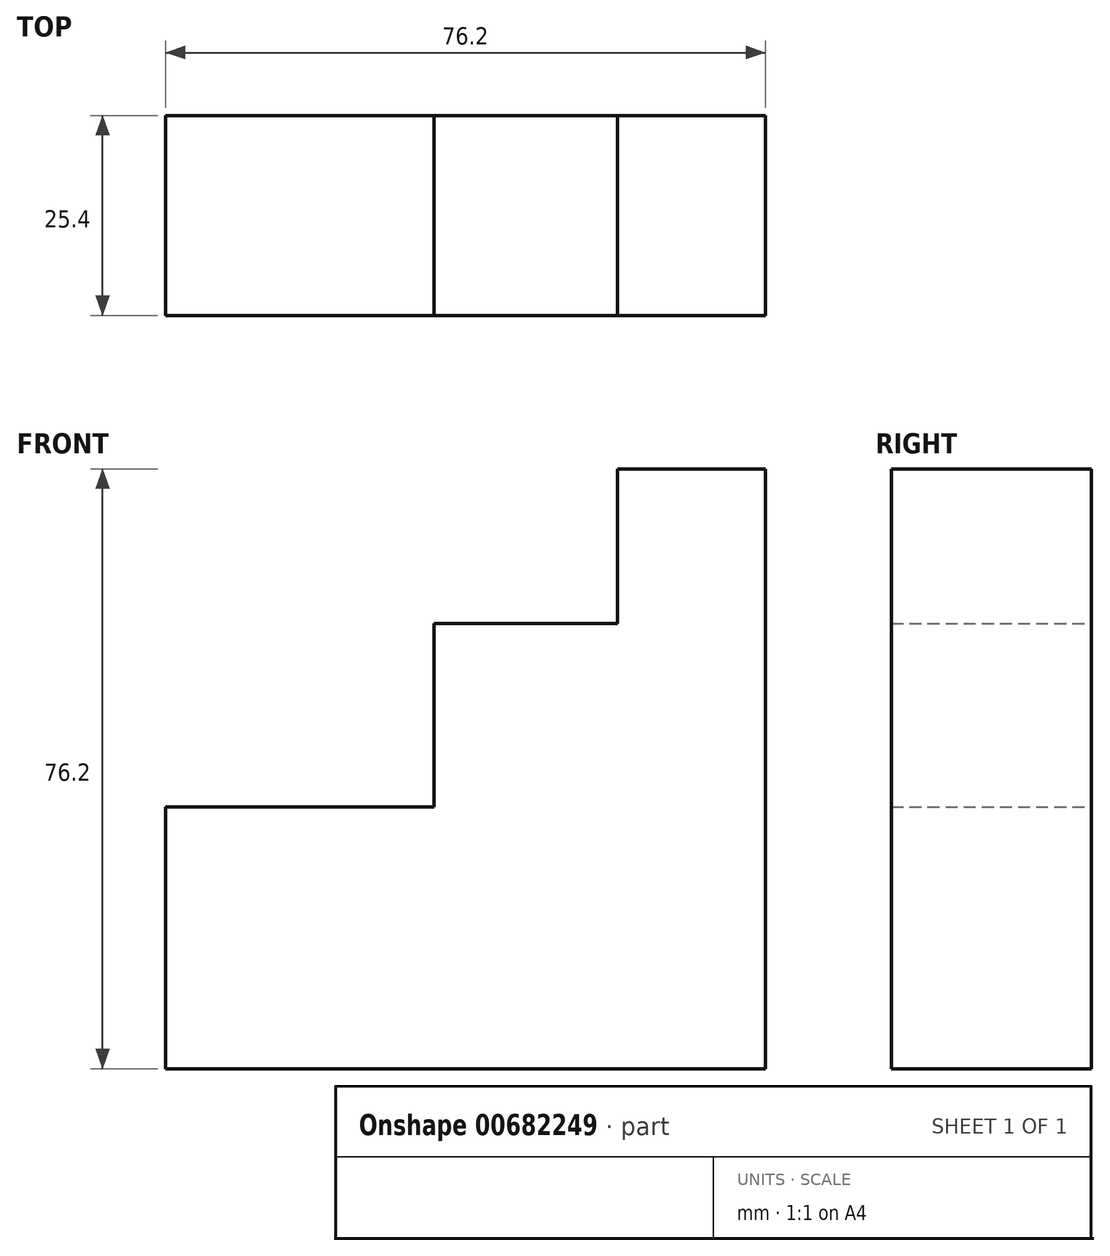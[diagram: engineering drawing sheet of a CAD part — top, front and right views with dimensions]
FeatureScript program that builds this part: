
annotation { "Feature Type Name" : "Feature", "Feature Type Description" : "" }
export const myFeature = defineFeature(function(context is Context, id is Id, definition is map)
    precondition{}
    {
        {
            var Q0;
            Q0=qCreatedBy(makeId("Front.planeOp"),FACE);
            var sketch = newSketch(context, id + "F0", { "sketchPlane" : qUnion([Q0])});
            skLineSegment(sketch, "E0", {"start": v(0, 0) * mm, "end": v(76.2, 0) * mm});
            skLineSegment(sketch, "E1", {"start": v(76.2, 0) * mm, "end": v(76.2, 76.2) * mm});
            skLineSegment(sketch, "E2", {"start": v(76.2, 76.2) * mm, "end": v(57.42, 76.2) * mm});
            skLineSegment(sketch, "E3", {"start": v(57.42, 76.2) * mm, "end": v(57.42, 56.55) * mm});
            skLineSegment(sketch, "E4", {"start": v(57.42, 56.55) * mm, "end": v(34.1, 56.55) * mm});
            skLineSegment(sketch, "E5", {"start": v(34.1, 56.55) * mm, "end": v(34.1, 33.24) * mm});
            skLineSegment(sketch, "E6", {"start": v(34.1, 33.24) * mm, "end": v(0, 33.24) * mm});
            skLineSegment(sketch, "E7", {"start": v(0, 33.24) * mm, "end": v(0, 0) * mm});
            skSolve(sketch);
        }
        {
            var Q0;
            Q0 = qSketchRegion(id + "F0", true);
            extrude(context, id + "F1", {"entities" : qUnion([Q0]), "depth" : 25.4 * mm, "offsetDistance" : 25.4 * mm});
        }
    });
